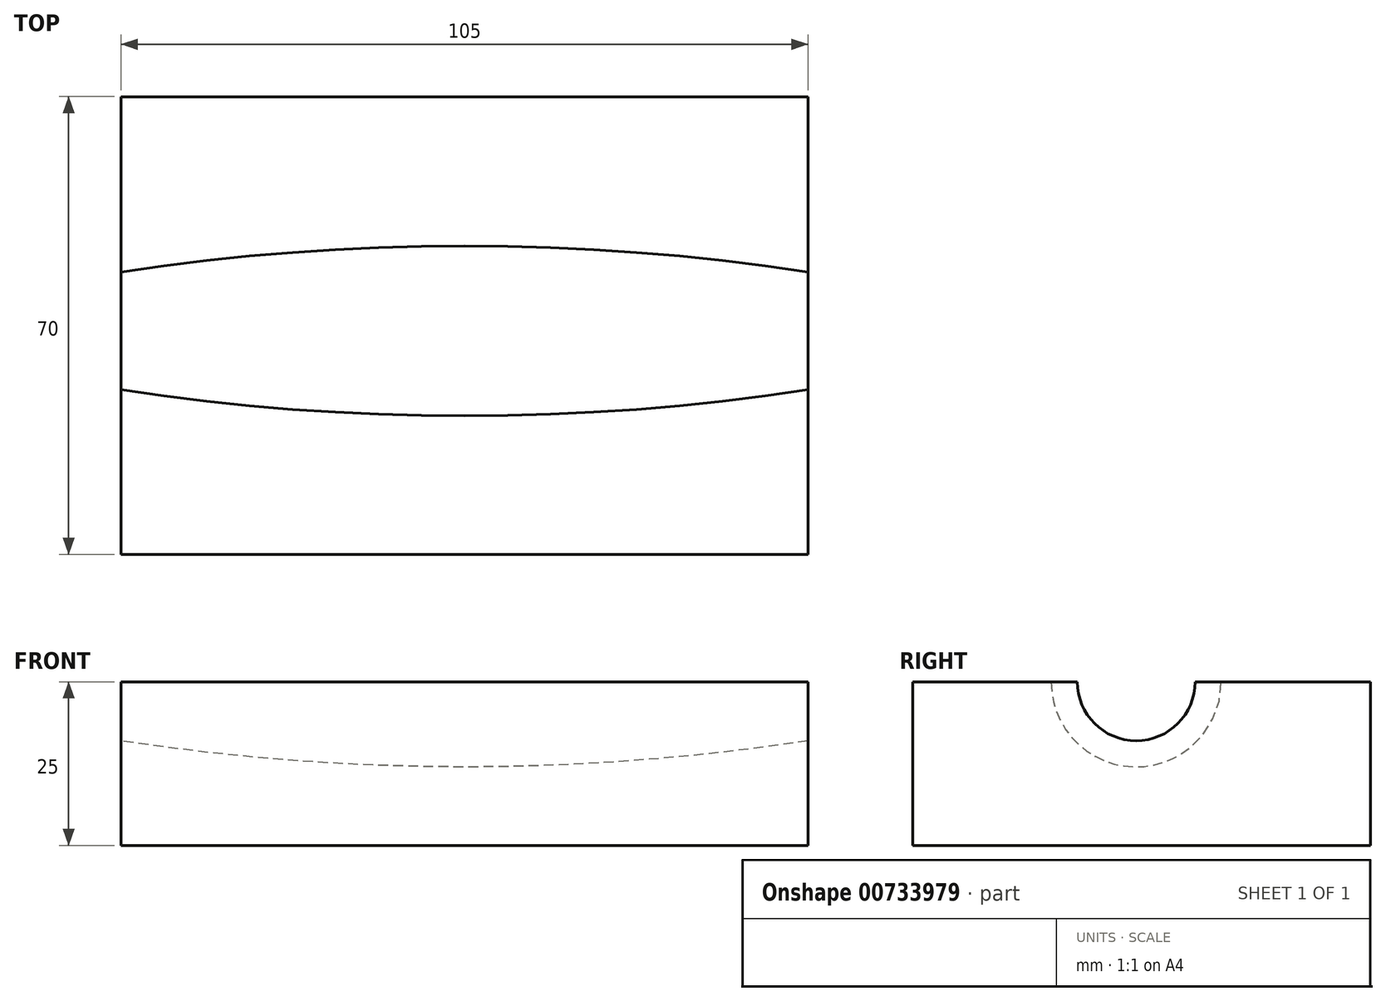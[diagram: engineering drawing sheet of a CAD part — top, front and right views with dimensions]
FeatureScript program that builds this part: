
annotation { "Feature Type Name" : "Feature", "Feature Type Description" : "" }
export const myFeature = defineFeature(function(context is Context, id is Id, definition is map)
    precondition{}
    {
        {
            var Q0;
            Q0=qCreatedBy(makeId("Front.planeOp"),FACE);
            var sketch = newSketch(context, id + "F0", { "sketchPlane" : qUnion([Q0])});
            skLineSegment(sketch, "E0", {"start": v(-90.68, 0) * mm, "end": v(100.6, 0) * mm, "construction": true});
            skLineSegment(sketch, "E1", {"start": v(-52.5, 0) * mm, "end": v(-52.5, 9) * mm});
            skLineSegment(sketch, "E2", {"start": v(52.5, 0) * mm, "end": v(52.5, 9) * mm});
            skLineSegment(sketch, "E3", {"start": v(-52.5, 0) * mm, "end": v(52.5, 0) * mm});
            skLineSegment(sketch, "E4", {"start": v(0, 0) * mm, "end": v(0, 13) * mm, "construction": true});
            skArc(sketch, "E5", {"start": v(52.5, 9) * mm, "mid": v(0, 13) * mm, "end": v(-52.5, 9) * mm});
            skSolve(sketch);
        }
        {
            var Q0;
            Q0=qCreatedBy(makeId("Top.planeOp"),FACE);
            var sketch = newSketch(context, id + "F1", { "sketchPlane" : qUnion([Q0])});
            skLineSegment(sketch, "E6.bottom", {"start": v(-52.5, 35.82) * mm, "end": v(52.5, 35.82) * mm});
            skLineSegment(sketch, "E6.top", {"start": v(-52.5, -34.18) * mm, "end": v(52.5, -34.18) * mm});
            skLineSegment(sketch, "E6.left", {"start": v(-52.5, 35.82) * mm, "end": v(-52.5, -34.18) * mm});
            skLineSegment(sketch, "E6.right", {"start": v(52.5, 35.82) * mm, "end": v(52.5, -34.18) * mm});
            skSolve(sketch);
        }
        {
            var Q0;
            Q0=qSketchRegion(id+"F1",true);
            extrude(context, id + "F2", {"entities" : qUnion([Q0]), "oppositeDirection" : true, "depth" : 25 * mm, "offsetDistance" : 25 * mm});
        }
        {
            var Q0;
            Q0=makeQuery(id+"F0.imprint","IMPRINT",FACE,{"disambiguationData":[TD([[makeQuery(id+"F0.imprint","IMPRINT",EDGE,{"derivedFrom":sQuery(id+"F0.wireOp",EDGE,"E1")}),-1.0]])]});
            var Q1;
            Q1=sQuery(id+"F0.wireOp",EDGE,"E0");
            revolve(context, id + "F3", {"operationType" : NewBodyOperationType.REMOVE, "surfaceOperationType" : NewSurfaceOperationType.NEW, "entities" : qUnion([Q0]), "axis" : qUnion([Q1]), "revolveType" : RevolveType.FULL, "oppositeDirection" : true});
        }
        {
            var Q0;
            Q0=makeQuery(id+"F2.opExtrude","SWEPT_BODY",BODY,{"disambiguationData":[OSD([sQuery(id+"F1.wireOp",EDGE,"E6.bottom"),sQuery(id+"F1.wireOp",EDGE,"E6.top"),sQuery(id+"F1.wireOp",EDGE,"E6.left"),sQuery(id+"F1.wireOp",EDGE,"E6.right")])]});
            var Q1;
            {var subQ0=sQuery(id+"F1.wireOp",EDGE,"E6.bottom");var subQ1=sQuery(id+"F1.wireOp",EDGE,"E6.right");Q1=makeQuery(id+"F3.boolean.opBoolean","SPLIT",EDGE,{"disambiguationData":[TD([makeQuery(id+"F2.opExtrude","SWEPT_FACE",FACE,{"disambiguationData":[OSD([subQ0])]})])],"derivedFrom":makeQuery(id+"F2.opExtrude","CAP_EDGE",EDGE,{"disambiguationData":[OSD([subQ1])],"isStart":true})});}
            transform(context, id + "F4", {"entities" : qUnion([Q0]), "transformType" : TransformType.ROTATION, "transformAxis" : qUnion([Q1]), "angle" : 180 * degree, "oppositeDirection" : true, "makeCopy" : true});
        }
        {
            var Q0;
            Q0=makeQuery(id+"F4.opPattern","COPY",BODY,{"derivedFrom":makeQuery(id+"F2.opExtrude","SWEPT_BODY",BODY,{"disambiguationData":[OSD([sQuery(id+"F1.wireOp",EDGE,"E6.bottom"),sQuery(id+"F1.wireOp",EDGE,"E6.top"),sQuery(id+"F1.wireOp",EDGE,"E6.left"),sQuery(id+"F1.wireOp",EDGE,"E6.right")])]}),"instanceName":"1"});
            deleteBodies(context, id + "F5", {"entities" : qUnion([Q0])});
        }
    });
